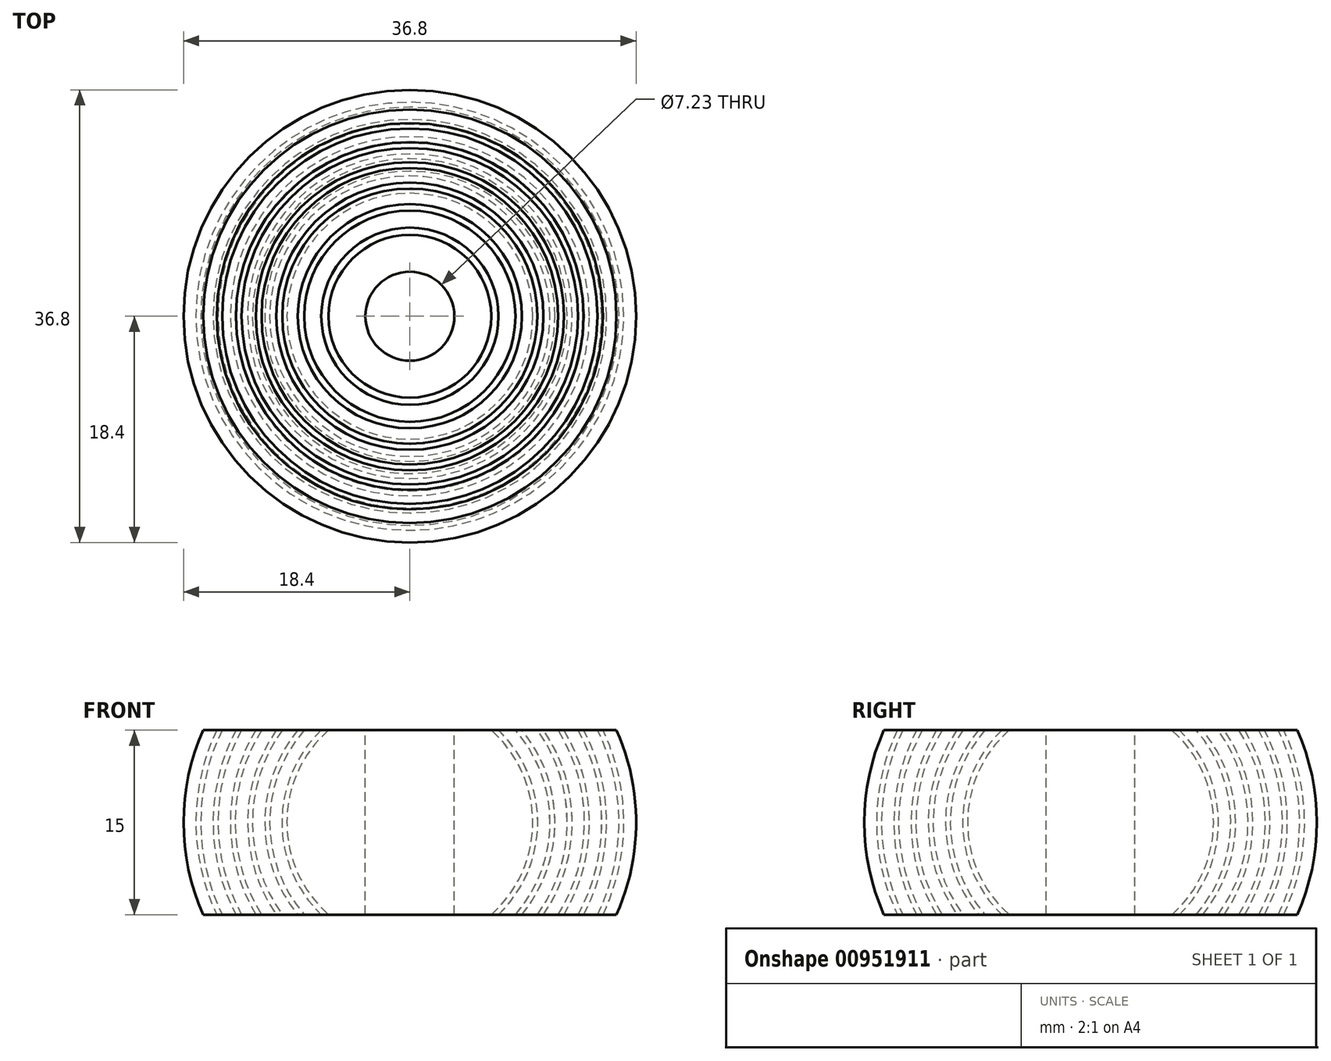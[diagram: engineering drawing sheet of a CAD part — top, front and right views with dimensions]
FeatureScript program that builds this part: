
annotation { "Feature Type Name" : "Feature", "Feature Type Description" : "" }
export const myFeature = defineFeature(function(context is Context, id is Id, definition is map)
    precondition{}
    {
        {
            var Q0;
            Q0=qCreatedBy(makeId("Front.planeOp"),FACE);
            var sketch = newSketch(context, id + "F0", { "sketchPlane" : qUnion([Q0])});
            skArc(sketch, "E0", {"start": v(-6.61, 7.5) * mm, "mid": v(-10, 0) * mm, "end": v(-6.61, -7.5) * mm});
            skArc(sketch, "E1", {"start": v(-7.2, 7.5) * mm, "mid": v(-10.4, 0) * mm, "end": v(-7.2, -7.5) * mm});
            skArc(sketch, "E2", {"start": v(-8.59, 7.5) * mm, "mid": v(-11.4, 0) * mm, "end": v(-8.59, -7.5) * mm});
            skArc(sketch, "E3", {"start": v(-9.1, 7.5) * mm, "mid": v(-11.8, 0) * mm, "end": v(-9.1, -7.5) * mm});
            skArc(sketch, "E4", {"start": v(-10.37, 7.5) * mm, "mid": v(-12.8, 0) * mm, "end": v(-10.37, -7.5) * mm});
            skArc(sketch, "E5", {"start": v(-10.86, 7.5) * mm, "mid": v(-13.2, 0) * mm, "end": v(-10.86, -7.5) * mm});
            skArc(sketch, "E6", {"start": v(-12.06, 7.5) * mm, "mid": v(-14.2, 0) * mm, "end": v(-12.06, -7.5) * mm});
            skArc(sketch, "E7", {"start": v(-12.53, 7.5) * mm, "mid": v(-14.6, 0) * mm, "end": v(-12.53, -7.5) * mm});
            skArc(sketch, "E8", {"start": v(-13.68, 7.5) * mm, "mid": v(-15.6, 0) * mm, "end": v(-13.68, -7.5) * mm});
            skArc(sketch, "E9", {"start": v(-14.13, 7.5) * mm, "mid": v(-16, 0) * mm, "end": v(-14.13, -7.5) * mm});
            skArc(sketch, "E10", {"start": v(-15.26, 7.5) * mm, "mid": v(-17, 0) * mm, "end": v(-15.26, -7.5) * mm});
            skLineSegment(sketch, "E11", {"start": v(-15.26, -7.5) * mm, "end": v(15.26, -7.5) * mm});
            skLineSegment(sketch, "E12", {"start": v(15.26, -7.5) * mm, "end": v(15.26, 7.5) * mm, "construction": true});
            skLineSegment(sketch, "E13", {"start": v(15.26, 7.5) * mm, "end": v(-15.26, 7.5) * mm});
            skLineSegment(sketch, "E14", {"start": v(0, 7.5) * mm, "end": v(0, -7.5) * mm});
            skArc(sketch, "E15.trimOffspring", {"start": v(15.26, -7.5) * mm, "mid": v(17, 0) * mm, "end": v(15.26, 7.5) * mm});
            skArc(sketch, "E16.trimOffspring", {"start": v(14.13, -7.5) * mm, "mid": v(16, 0) * mm, "end": v(14.13, 7.5) * mm});
            skArc(sketch, "E17.trimOffspring", {"start": v(13.68, -7.5) * mm, "mid": v(15.6, 0) * mm, "end": v(13.68, 7.5) * mm});
            skArc(sketch, "E18.trimOffspring", {"start": v(12.53, -7.5) * mm, "mid": v(14.6, 0) * mm, "end": v(12.53, 7.5) * mm});
            skArc(sketch, "E19.trimOffspring", {"start": v(12.06, -7.5) * mm, "mid": v(14.2, 0) * mm, "end": v(12.06, 7.5) * mm});
            skArc(sketch, "E20.trimOffspring", {"start": v(10.86, -7.5) * mm, "mid": v(13.2, 0) * mm, "end": v(10.86, 7.5) * mm});
            skArc(sketch, "E21.trimOffspring", {"start": v(10.37, -7.5) * mm, "mid": v(12.8, 0) * mm, "end": v(10.37, 7.5) * mm});
            skArc(sketch, "E22.trimOffspring", {"start": v(9.1, -7.5) * mm, "mid": v(11.8, 0) * mm, "end": v(9.1, 7.5) * mm});
            skArc(sketch, "E23.trimOffspring", {"start": v(8.59, -7.5) * mm, "mid": v(11.4, 0) * mm, "end": v(8.59, 7.5) * mm});
            skArc(sketch, "E24.trimOffspring", {"start": v(7.2, -7.5) * mm, "mid": v(10.4, 0) * mm, "end": v(7.2, 7.5) * mm});
            skArc(sketch, "E25.trimOffspring", {"start": v(6.61, -7.5) * mm, "mid": v(10, 0) * mm, "end": v(6.61, 7.5) * mm});
            skLineSegment(sketch, "E26", {"start": v(3.61, 7.5) * mm, "end": v(3.61, -7.5) * mm});
            skArc(sketch, "E27", {"start": v(-15.7, 7.5) * mm, "mid": v(-17.4, 0) * mm, "end": v(-15.7, -7.5) * mm});
            skArc(sketch, "E28", {"start": v(-16.8, 7.5) * mm, "mid": v(-18.4, 0) * mm, "end": v(-16.8, -7.5) * mm});
            skLineSegment(sketch, "E29", {"start": v(-15.26, 7.5) * mm, "end": v(-16.8, 7.5) * mm});
            skLineSegment(sketch, "E30", {"start": v(-15.26, -7.5) * mm, "end": v(-16.8, -7.5) * mm});
            skLineSegment(sketch, "E31", {"start": v(15.26, 7.5) * mm, "end": v(16.8, 7.5) * mm});
            skLineSegment(sketch, "E32", {"start": v(15.26, -7.5) * mm, "end": v(16.8, -7.5) * mm});
            skArc(sketch, "E33.trimOffspring", {"start": v(15.7, -7.5) * mm, "mid": v(17.4, 0) * mm, "end": v(15.7, 7.5) * mm});
            skArc(sketch, "E34.trimOffspring", {"start": v(16.8, -7.5) * mm, "mid": v(18.4, 0) * mm, "end": v(16.8, 7.5) * mm});
            skSolve(sketch);
        }
        {
            var Q0;
            {var subQ0=sQuery(id+"F0.wireOp",EDGE,"E25.trimOffspring");Q0=makeQuery(id+"F0.imprint","IMPRINT",FACE,{"disambiguationData":[TD([[makeQuery(id+"F0.imprint","IMPRINT",EDGE,{"derivedFrom":subQ0}),1.0]])]});}
            var Q1;
            {var subQ0=sQuery(id+"F0.wireOp",EDGE,"E23.trimOffspring");Q1=makeQuery(id+"F0.imprint","IMPRINT",FACE,{"disambiguationData":[TD([[makeQuery(id+"F0.imprint","IMPRINT",EDGE,{"derivedFrom":subQ0}),1.0]])]});}
            var Q2;
            {var subQ0=sQuery(id+"F0.wireOp",EDGE,"E21.trimOffspring");Q2=makeQuery(id+"F0.imprint","IMPRINT",FACE,{"disambiguationData":[TD([[makeQuery(id+"F0.imprint","IMPRINT",EDGE,{"derivedFrom":subQ0}),1.0]])]});}
            var Q3;
            {var subQ0=sQuery(id+"F0.wireOp",EDGE,"E19.trimOffspring");Q3=makeQuery(id+"F0.imprint","IMPRINT",FACE,{"disambiguationData":[TD([[makeQuery(id+"F0.imprint","IMPRINT",EDGE,{"derivedFrom":subQ0}),1.0]])]});}
            var Q4;
            {var subQ0=sQuery(id+"F0.wireOp",EDGE,"E17.trimOffspring");Q4=makeQuery(id+"F0.imprint","IMPRINT",FACE,{"disambiguationData":[TD([[makeQuery(id+"F0.imprint","IMPRINT",EDGE,{"derivedFrom":subQ0}),1.0]])]});}
            var Q5;
            {var subQ0=sQuery(id+"F0.wireOp",EDGE,"E15.trimOffspring");Q5=makeQuery(id+"F0.imprint","IMPRINT",FACE,{"disambiguationData":[TD([[makeQuery(id+"F0.imprint","IMPRINT",EDGE,{"derivedFrom":subQ0}),1.0]])]});}
            var Q6;
            {var subQ2=sQuery(id+"F0.wireOp",EDGE,"E33.trimOffspring");Q6=makeQuery(id+"F0.imprint","IMPRINT",FACE,{"disambiguationData":[TD([[makeQuery(id+"F0.imprint","IMPRINT",EDGE,{"derivedFrom":subQ2}),-1.0]])]});}
            var Q7;
            Q7=sQuery(id+"F0.wireOp",EDGE,"E14");
            revolve(context, id + "F1", {"surfaceOperationType" : NewSurfaceOperationType.NEW, "entities" : qUnion([Q0, Q1, Q2, Q3, Q4, Q5, Q6]), "axis" : qUnion([Q7]), "revolveType" : RevolveType.FULL});
        }
    });
